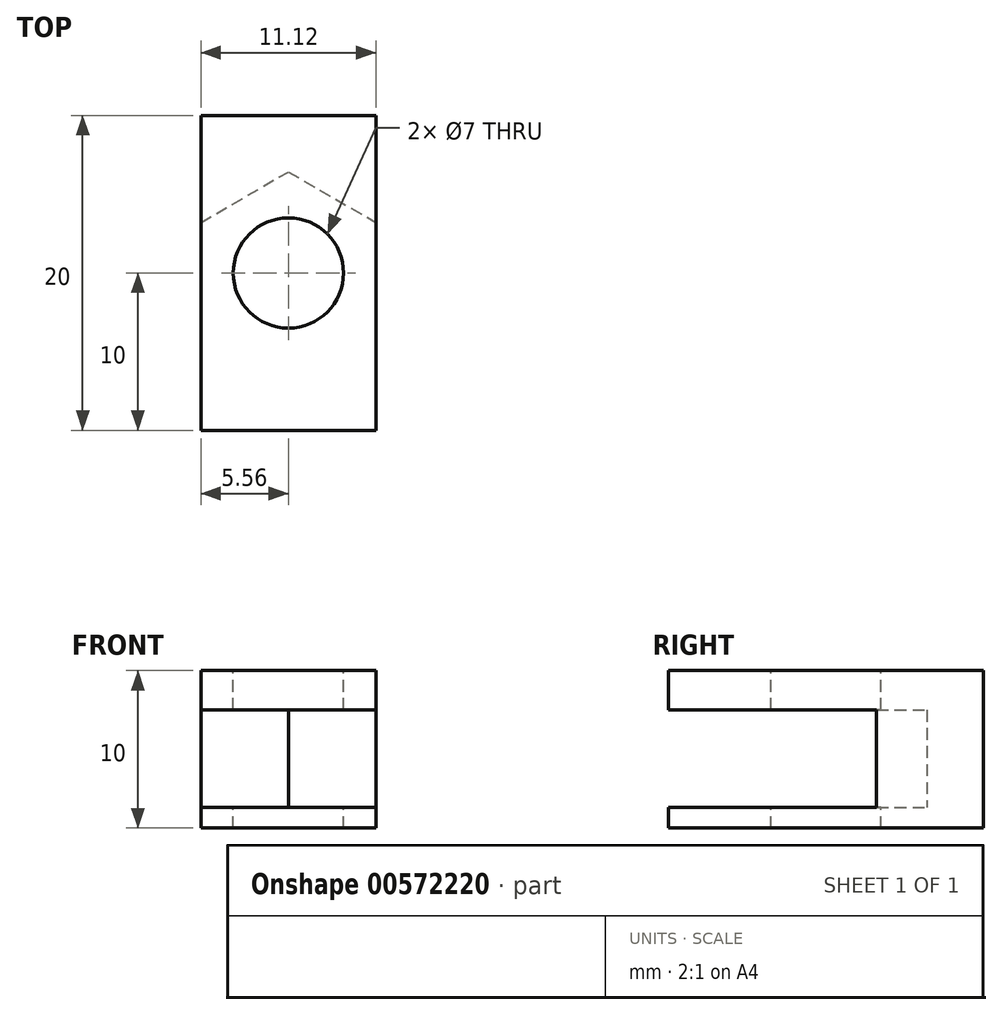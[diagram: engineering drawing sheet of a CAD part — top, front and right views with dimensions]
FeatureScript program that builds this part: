
annotation { "Feature Type Name" : "Feature", "Feature Type Description" : "" }
export const myFeature = defineFeature(function(context is Context, id is Id, definition is map)
    precondition{}
    {
        {
            var Q0;
            Q0=qCreatedBy(makeId("Top.planeOp"),FACE);
            var sketch = newSketch(context, id + "F0", { "sketchPlane" : qUnion([Q0])});
            skLineSegment(sketch, "E0.bottom", {"start": v(-75, 10) * mm, "end": v(75, 10) * mm});
            skLineSegment(sketch, "E0.top", {"start": v(-75, -10) * mm, "end": v(75, -10) * mm});
            skLineSegment(sketch, "E0.left", {"start": v(-75, 10) * mm, "end": v(-75, -10) * mm});
            skLineSegment(sketch, "E0.right", {"start": v(75, 10) * mm, "end": v(75, -10) * mm});
            skPoint(sketch, "E0.middle", {"position": v(0, 0) * mm});
            skCircle(sketch, "E1.cCircle", {"center": v(0, 0) * mm, "radius": 5.56 * mm, "construction": true});
            skLineSegment(sketch, "E1.0", {"start": v(0, 6.42) * mm, "end": v(5.56, 3.21) * mm});
            skLineSegment(sketch, "E1.1", {"start": v(5.56, 3.21) * mm, "end": v(5.56, -3.21) * mm});
            skLineSegment(sketch, "E1.2", {"start": v(5.56, -3.21) * mm, "end": v(0, -6.42) * mm});
            skLineSegment(sketch, "E1.3", {"start": v(0, -6.42) * mm, "end": v(-5.56, -3.21) * mm});
            skLineSegment(sketch, "E1.4", {"start": v(-5.56, -3.21) * mm, "end": v(-5.56, 3.21) * mm});
            skLineSegment(sketch, "E1.5", {"start": v(-5.56, 3.21) * mm, "end": v(0, 6.42) * mm});
            skPoint(sketch, "E1.0.midPoint", {"position": v(2.78, 4.82) * mm});
            skLineSegment(sketch, "E2", {"start": v(-65, 0) * mm, "end": v(65, 0) * mm, "construction": true});
            skLineSegment(sketch, "E3", {"start": v(-55, 0) * mm, "end": v(55, 0) * mm, "construction": true});
            skLineSegment(sketch, "E4.bottom", {"start": v(5.56, 3.21) * mm, "end": v(-5.56, 3.21) * mm});
            skLineSegment(sketch, "E4.top", {"start": v(5.56, 10) * mm, "end": v(-5.56, 10) * mm});
            skLineSegment(sketch, "E4.left", {"start": v(5.56, 3.21) * mm, "end": v(5.56, 10) * mm});
            skLineSegment(sketch, "E4.right", {"start": v(-5.56, 3.21) * mm, "end": v(-5.56, 10) * mm});
            skLineSegment(sketch, "E5.bottom", {"start": v(5.56, -3.21) * mm, "end": v(-5.56, -3.21) * mm});
            skLineSegment(sketch, "E5.top", {"start": v(5.56, -10) * mm, "end": v(-5.56, -10) * mm});
            skLineSegment(sketch, "E5.left", {"start": v(5.56, -3.21) * mm, "end": v(5.56, -10) * mm});
            skLineSegment(sketch, "E5.right", {"start": v(-5.56, -3.21) * mm, "end": v(-5.56, -10) * mm});
            skSolve(sketch);
        }
        {
            var Q0;
            Q0=makeQuery(id+"F0.imprint","IMPRINT",FACE,{"disambiguationData":[TD([[makeQuery(id+"F0.imprint","IMPRINT",EDGE,{"derivedFrom":sQuery(id+"F0.wireOp",EDGE,"E0.bottom")}),-1.0]])]});
            var Q1;
            Q1=makeQuery(id+"F0.imprint","IMPRINT",FACE,{"disambiguationData":[TD([[makeQuery(id+"F0.imprint","IMPRINT",EDGE,{"derivedFrom":sQuery(id+"F0.wireOp",EDGE,"E1.0")}),-1.0]])]});
            var Q2;
            Q2=makeQuery(id+"F0.imprint","IMPRINT",FACE,{"disambiguationData":[TD([[makeQuery(id+"F0.imprint","IMPRINT",EDGE,{"derivedFrom":sQuery(id+"F0.wireOp",EDGE,"E1.0")}),1.0]])]});
            var Q3;
            Q3=makeQuery(id+"F0.imprint","IMPRINT",FACE,{"disambiguationData":[TD([[makeQuery(id+"F0.imprint","IMPRINT",EDGE,{"derivedFrom":sQuery(id+"F0.wireOp",EDGE,"E1.2")}),1.0]])]});
            var Q4;
            Q4=makeQuery(id+"F0.imprint","IMPRINT",FACE,{"disambiguationData":[TD([[makeQuery(id+"F0.imprint","IMPRINT",EDGE,{"derivedFrom":sQuery(id+"F0.wireOp",EDGE,"E1.2")}),-1.0]])]});
            var Q5;
            Q5=makeQuery(id+"F0.imprint","IMPRINT",FACE,{"disambiguationData":[TD([[makeQuery(id+"F0.imprint","IMPRINT",EDGE,{"derivedFrom":sQuery(id+"F0.wireOp",EDGE,"E1.1")}),-1.0]])]});
            extrude(context, id + "F1", {"entities" : qUnion([Q0, Q1, Q2, Q3, Q4, Q5]), "depth" : 5 * mm, "offsetDistance" : 25 * mm, "hasSecondDirection" : true, "secondDirectionOppositeDirection" : true, "secondDirectionDepth" : 5 * mm});
        }
        {
            var Q0;
            Q0=sQuery(id+"F0.wireOp",VERTEX,"E3.start");
            var Q1;
            Q1=sQuery(id+"F0.wireOp",VERTEX,"E3.end");
            var Q2;
            Q2=sQuery(id+"F0.wireOp",VERTEX,"E0.middle");
            var Q3;
            Q3=makeQuery(id+"F1.opExtrude","SWEPT_BODY",BODY,{"disambiguationData":[OSD([sQuery(id+"F0.wireOp",EDGE,"E0.bottom"),sQuery(id+"F0.wireOp",EDGE,"E0.top"),sQuery(id+"F0.wireOp",EDGE,"E0.left"),sQuery(id+"F0.wireOp",EDGE,"E0.right"),sQuery(id+"F0.wireOp",EDGE,"E4.top"),sQuery(id+"F0.wireOp",EDGE,"E5.top")])]});
            hole(context, id + "F2", {"style" : HoleStyle.SIMPLE, "endStyle" : HoleEndStyle.THROUGH, "holeDiameter" : 7 * mm, "majorDiameter" : 5 * mm, "isTappedThrough" : true, "tappedDepth" : 10.5 * mm, "tapClearance" : 3, "locations" : qUnion([Q0, Q1, Q2]), "scope" : qUnion([Q3])});
        }
        {
            var Q0;
            Q0=sQuery(id+"F0.wireOp",VERTEX,"E3.end");
            var Q1;
            Q1=sQuery(id+"F0.wireOp",VERTEX,"E3.start");
            var Q2;
            Q2=sQuery(id+"F0.wireOp",VERTEX,"E0.middle");
            var Q3;
            Q3=makeQuery(id+"F1.opExtrude","SWEPT_BODY",BODY,{"disambiguationData":[OSD([sQuery(id+"F0.wireOp",EDGE,"E0.bottom"),sQuery(id+"F0.wireOp",EDGE,"E0.top"),sQuery(id+"F0.wireOp",EDGE,"E0.left"),sQuery(id+"F0.wireOp",EDGE,"E0.right"),sQuery(id+"F0.wireOp",EDGE,"E4.top"),sQuery(id+"F0.wireOp",EDGE,"E5.top")])]});
            hole(context, id + "F3", {"style" : HoleStyle.SIMPLE, "endStyle" : HoleEndStyle.THROUGH, "oppositeDirection" : true, "holeDiameter" : 7 * mm, "majorDiameter" : 5 * mm, "isTappedThrough" : true, "tappedDepth" : 10.5 * mm, "tapClearance" : 3, "locations" : qUnion([Q0, Q1, Q2]), "scope" : qUnion([Q3])});
        }
        {
            var Q0;
            Q0=makeQuery(id+"F0.imprint","IMPRINT",FACE,{"disambiguationData":[TD([[makeQuery(id+"F0.imprint","IMPRINT",EDGE,{"derivedFrom":sQuery(id+"F0.wireOp",EDGE,"E1.0")}),-1.0]])]});
            var Q1;
            Q1=makeQuery(id+"F0.imprint","IMPRINT",FACE,{"disambiguationData":[TD([[makeQuery(id+"F0.imprint","IMPRINT",EDGE,{"derivedFrom":sQuery(id+"F0.wireOp",EDGE,"E1.1")}),-1.0]])]});
            var Q2;
            Q2=makeQuery(id+"F0.imprint","IMPRINT",FACE,{"disambiguationData":[TD([[makeQuery(id+"F0.imprint","IMPRINT",EDGE,{"derivedFrom":sQuery(id+"F0.wireOp",EDGE,"E1.2")}),-1.0]])]});
            var Q3;
            Q3=makeQuery(id+"F0.imprint","IMPRINT",FACE,{"disambiguationData":[TD([[makeQuery(id+"F0.imprint","IMPRINT",EDGE,{"derivedFrom":sQuery(id+"F0.wireOp",EDGE,"E1.2")}),1.0]])]});
            extrude(context, id + "F4", {"entities" : qUnion([Q0, Q1, Q2, Q3]), "operationType" : NewBodyOperationType.REMOVE, "depth" : 2.5 * mm, "offsetDistance" : 25 * mm, "hasSecondDirection" : true, "secondDirectionOppositeDirection" : true, "secondDirectionDepth" : 3.7 * mm});
        }
    });
